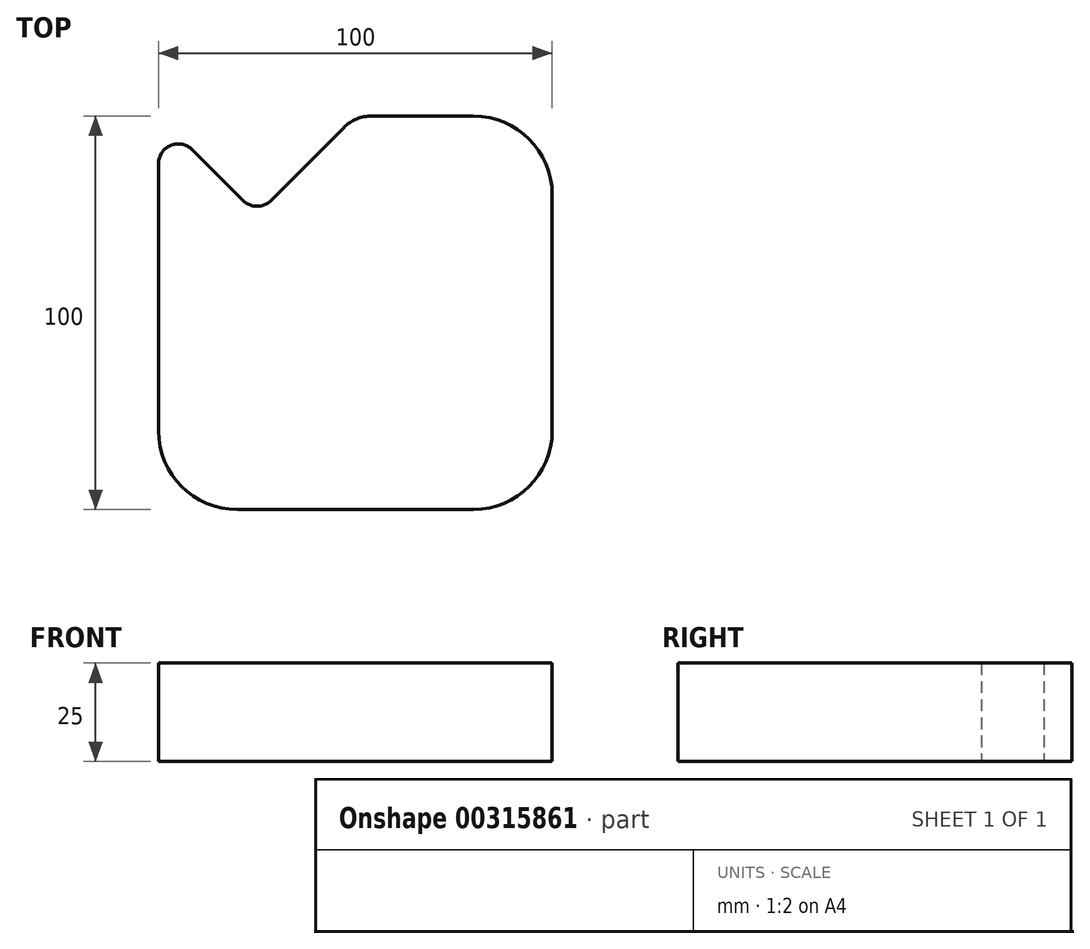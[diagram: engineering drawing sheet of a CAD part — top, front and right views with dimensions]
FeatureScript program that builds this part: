
annotation { "Feature Type Name" : "Feature", "Feature Type Description" : "" }
export const myFeature = defineFeature(function(context is Context, id is Id, definition is map)
    precondition{}
    {
        {
            var Q0;
            Q0=qCreatedBy(makeId("Top.planeOp"),FACE);
            var sketch = newSketch(context, id + "F0", { "sketchPlane" : qUnion([Q0])});
            skLineSegment(sketch, "E0.bottom", {"start": v(30, 50) * mm, "end": v(4.14, 50) * mm});
            skLineSegment(sketch, "E0.top", {"start": v(30, -50) * mm, "end": v(-30, -50) * mm});
            skLineSegment(sketch, "E0.left", {"start": v(50, 30) * mm, "end": v(50, -30) * mm});
            skLineSegment(sketch, "E0.right", {"start": v(-50, 37.93) * mm, "end": v(-50, -30) * mm});
            skPoint(sketch, "E0.middle", {"position": v(0, 0) * mm});
            skLineSegment(sketch, "E1", {"start": v(-41.46, 41.46) * mm, "end": v(-28.54, 28.54) * mm});
            skLineSegment(sketch, "E2", {"start": v(-2.93, 47.07) * mm, "end": v(-21.46, 28.54) * mm});
            skPoint(sketch, "E3.visualSharp", {"position": v(-50, 50) * mm});
            skArc(sketch, "E3.filletArc", {"start": v(-41.46, 41.46) * mm, "mid": v(-46.91, 42.55) * mm, "end": v(-50, 37.93) * mm});
            skPoint(sketch, "E4.visualSharp", {"position": v(-25, 25) * mm});
            skArc(sketch, "E4.filletArc", {"start": v(-28.54, 28.54) * mm, "mid": v(-25, 27.07) * mm, "end": v(-21.46, 28.54) * mm});
            skPoint(sketch, "E5.visualSharp", {"position": v(0, 50) * mm});
            skArc(sketch, "E5.filletArc", {"start": v(4.14, 50) * mm, "mid": v(0.32, 49.24) * mm, "end": v(-2.93, 47.07) * mm});
            skPoint(sketch, "E6.visualSharp", {"position": v(50, 50) * mm});
            skArc(sketch, "E6.filletArc", {"start": v(50, 30) * mm, "mid": v(44.14, 44.14) * mm, "end": v(30, 50) * mm});
            skPoint(sketch, "E7.visualSharp", {"position": v(50, -50) * mm});
            skArc(sketch, "E7.filletArc", {"start": v(30, -50) * mm, "mid": v(44.14, -44.14) * mm, "end": v(50, -30) * mm});
            skPoint(sketch, "E8.visualSharp", {"position": v(-50, -50) * mm});
            skArc(sketch, "E8.filletArc", {"start": v(-50, -30) * mm, "mid": v(-44.14, -44.14) * mm, "end": v(-30, -50) * mm});
            skSolve(sketch);
        }
        {
            var Q0;
            Q0=makeQuery(id+"F0.imprint","IMPRINT",FACE,{"disambiguationData":[TD([[makeQuery(id+"F0.imprint","IMPRINT",EDGE,{"derivedFrom":sQuery(id+"F0.wireOp",EDGE,"E0.bottom")}),1.0]])]});
            extrude(context, id + "F1", {"entities" : qUnion([Q0]), "depth" : 25 * mm});
        }
    });
